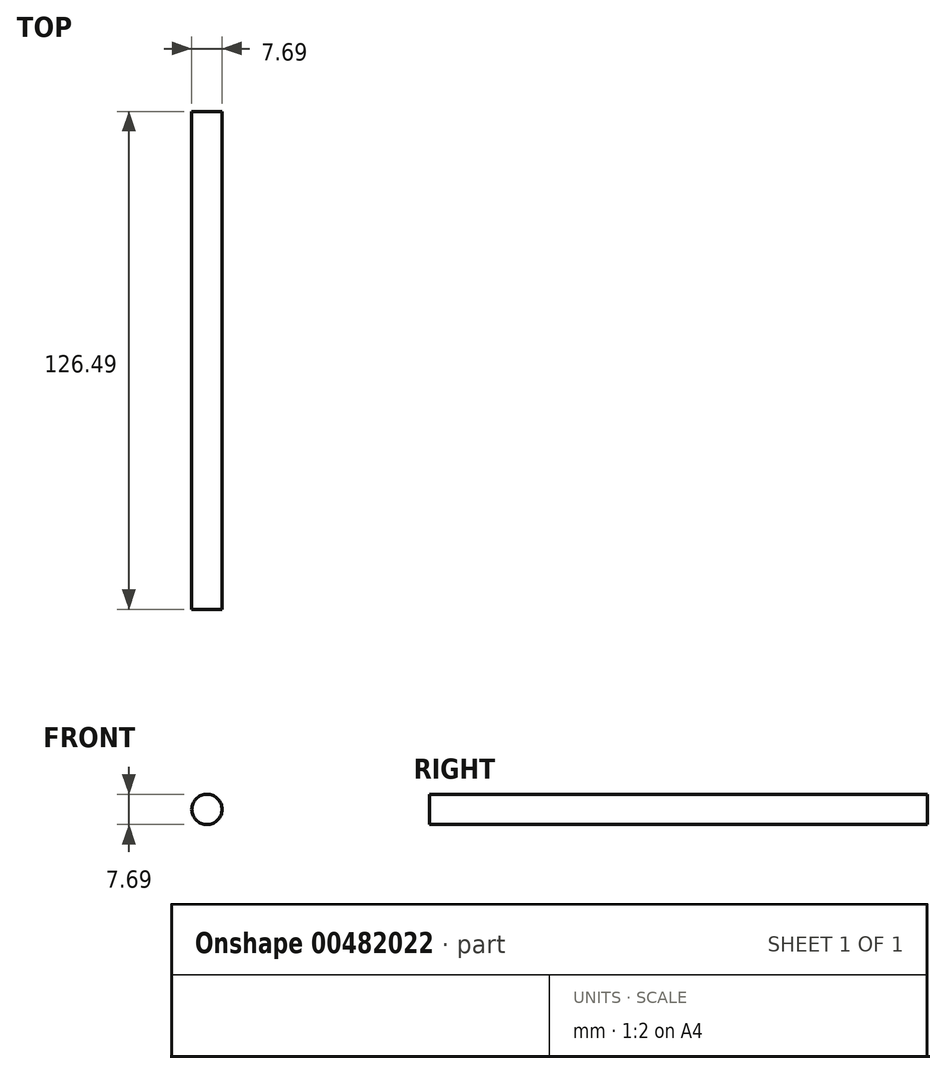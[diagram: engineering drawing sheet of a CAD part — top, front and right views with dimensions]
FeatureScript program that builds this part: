
annotation { "Feature Type Name" : "Feature", "Feature Type Description" : "" }
export const myFeature = defineFeature(function(context is Context, id is Id, definition is map)
    precondition{}
    {
        {
            var Q0;
            Q0=qCreatedBy(makeId("Front.planeOp"),FACE);
            var sketch = newSketch(context, id + "F0", { "sketchPlane" : qUnion([Q0])});
            skCircle(sketch, "E0", {"center": v(-6.02, 5.3) * mm, "radius": 8.02 * mm});
            skCircle(sketch, "E1", {"center": v(4.01, 13.61) * mm, "radius": 3.84 * mm});
            skSolve(sketch);
        }
        {
            var Q0;
            Q0=makeQuery(id+"F0.imprint","IMPRINT",FACE,{"disambiguationData":[TD([[makeQuery(id+"F0.imprint","IMPRINT",EDGE,{"derivedFrom":sQuery(id+"F0.wireOp",EDGE,"E1")}),1.0]])]});
            extrude(context, id + "F1", {"entities" : qUnion([Q0]), "oppositeDirection" : true, "depth" : 126.5 * mm});
        }
    });
